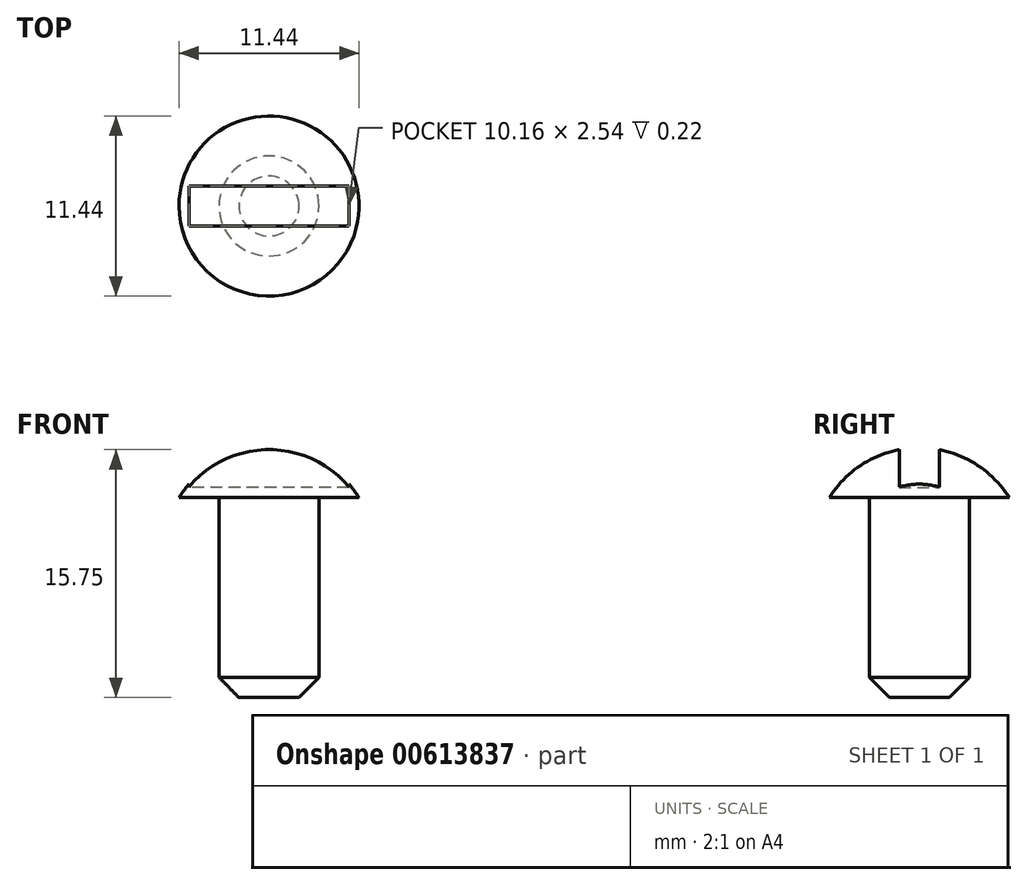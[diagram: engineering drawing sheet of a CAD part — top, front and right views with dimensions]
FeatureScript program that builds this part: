
annotation { "Feature Type Name" : "Feature", "Feature Type Description" : "" }
export const myFeature = defineFeature(function(context is Context, id is Id, definition is map)
    precondition{}
    {
        {
            var Q0;
            Q0=qCreatedBy(makeId("Front.planeOp"),FACE);
            var sketch = newSketch(context, id + "F0", { "sketchPlane" : qUnion([Q0])});
            skLineSegment(sketch, "E0", {"start": v(0, 0) * mm, "end": v(3.17, 0) * mm});
            skLineSegment(sketch, "E1", {"start": v(3.17, 0) * mm, "end": v(3.17, 12.7) * mm});
            skLineSegment(sketch, "E2", {"start": v(3.17, 12.7) * mm, "end": v(5.72, 12.7) * mm});
            skLineSegment(sketch, "E3", {"start": v(0, 0) * mm, "end": v(0, 15.88) * mm});
            skArc(sketch, "E4", {"start": v(0, 15.88) * mm, "mid": v(3.27, 15.02) * mm, "end": v(5.72, 12.7) * mm});
            skSolve(sketch);
        }
        {
            var Q0;
            Q0=makeQuery(id+"F0.imprint","IMPRINT",FACE,{"disambiguationData":[TD([[makeQuery(id+"F0.imprint","IMPRINT",EDGE,{"derivedFrom":sQuery(id+"F0.wireOp",EDGE,"E0")}),1.0]])]});
            var Q1;
            Q1=sQuery(id+"F0.wireOp",EDGE,"E3");
            revolve(context, id + "F1", {"entities" : qUnion([Q0]), "axis" : qUnion([Q1]), "revolveType" : RevolveType.FULL});
        }
        {
            var Q0;
            Q0=makeQuery(id+"F1.opRevolve","SWEPT_FACE",FACE,{"disambiguationData":[OSD([sQuery(id+"F0.wireOp",EDGE,"E0")])]});
            chamfer(context, id + "F2", {"entities" : qUnion([Q0]), "width" : 1.27 * mm, "tangentPropagation" : true});
        }
        {
            var Q0;
            Q0=makeQuery(id+"F1.opRevolve","SWEPT_FACE",FACE,{"disambiguationData":[OSD([sQuery(id+"F0.wireOp",EDGE,"E2")])]});
            cPlane(context, id + "F3", {"entities" : qUnion([Q0]), "cplaneType" : CPlaneType.OFFSET, "offset" : 0.64 * mm, "oppositeDirection" : true, "width" : 152.4 * mm, "height" : 152.4 * mm});
        }
        {
            var Q0;
            Q0=qCreatedBy(id+"F3.planeOp",FACE);
            var sketch = newSketch(context, id + "F4", { "sketchPlane" : qUnion([Q0])});
            skLineSegment(sketch, "E5.bottom", {"start": v(5.08, 1.27) * mm, "end": v(-5.08, 1.27) * mm});
            skLineSegment(sketch, "E5.top", {"start": v(5.08, -1.27) * mm, "end": v(-5.08, -1.27) * mm});
            skLineSegment(sketch, "E5.left", {"start": v(5.08, 1.27) * mm, "end": v(5.08, -1.27) * mm});
            skLineSegment(sketch, "E5.right", {"start": v(-5.08, 1.27) * mm, "end": v(-5.08, -1.27) * mm});
            skPoint(sketch, "E5.middle", {"position": v(0, 0) * mm});
            skSolve(sketch);
        }
        {
            var Q0;
            Q0 = qSketchRegion(id + "F4", true);
            extrude(context, id + "F5", {"entities" : qUnion([Q0]), "operationType" : NewBodyOperationType.REMOVE, "endBound" : BoundingType.THROUGH_ALL, "oppositeDirection" : true, "depth" : 25.4 * mm, "offsetDistance" : 25.4 * mm});
        }
    });
